# Revit family: PVC701_CallTrans W-12 PVC
name_source: partatom
category: Specialty Equipment
units: mm (PartAtom-declared; Revit-internal decimal feet)

## family parameters
Cut with Voids When Loaded = No
OmniClass Number = 23.10.00.00
OmniClass Title = Site Products
Part Type = Normal
Room Calculation Point = No
Round Connector Dimension = Use Diameter
Shared = No
Work Plane-Based = No

## types (2) — shared parameters
Assembly Code = F1030
Description = PVC701 is 6" x 1/8" x 50' Earth Shield PVC  Caltrans w-1/2 waterstop.
Edition number = 1
Height = 2 "
Hydrophilic = No
Hydrophobic = Yes
Keynote = 13000
Manufacturer = J P Specialties Inc.
Materials = PVC
Model = PVC701
Product Guid = 27e5cdcc-cece-4d8c-947d-ca6b8ef269ba
Product Material = JP Specialties - Polyvinyl Chloride (PVC)
Product data url = www.bimmodeller.com/jpspecialties/products/Polyvinyl-Chloride-PVC-Waterstop
Telephone = 951-763-7077
URL = https://www.jpspecialties.com
Weight = 1.1 lbs/lft
Width = 5.25 "

## per-type parameters (varying)
| type | Certifications | z_Horizontal | z_Vertical |
| PVC701 - Horizontal | NSF 61, NSF 372, CRD C-572-74, ASTM D560 | Yes | No |
| PVC701 - Vertical | NSF 61, NSF 372, CRD C-572-74, ASTM D540 | No | Yes |

## geometry (parser evidence)
native form markers: Sweep x4
no freeform markers — native parametric forms only
